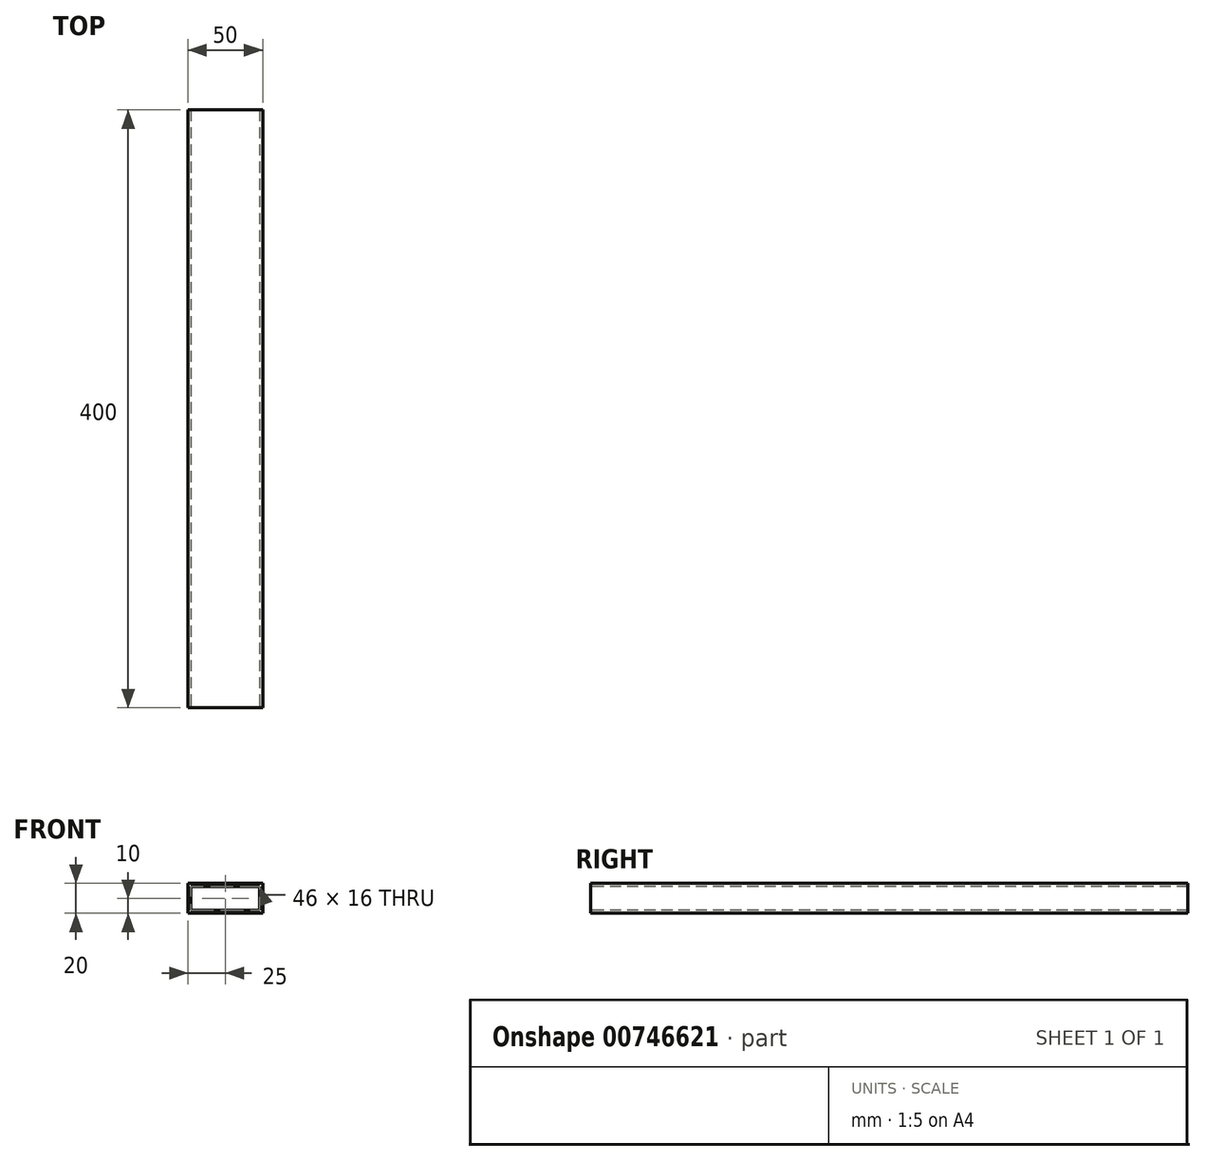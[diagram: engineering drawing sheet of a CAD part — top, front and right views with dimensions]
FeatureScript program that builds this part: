
annotation { "Feature Type Name" : "Feature", "Feature Type Description" : "" }
export const myFeature = defineFeature(function(context is Context, id is Id, definition is map)
    precondition{}
    {
        {
            var Q0;
            Q0=qCreatedBy(makeId("Front.planeOp"),FACE);
            var sketch = newSketch(context, id + "F0", { "sketchPlane" : qUnion([Q0])});
            skLineSegment(sketch, "E0.bottom", {"start": v(25, -10) * mm, "end": v(-25, -10) * mm});
            skLineSegment(sketch, "E0.top", {"start": v(25, 10) * mm, "end": v(-25, 10) * mm});
            skLineSegment(sketch, "E0.left", {"start": v(25, -10) * mm, "end": v(25, 10) * mm});
            skLineSegment(sketch, "E0.right", {"start": v(-25, -10) * mm, "end": v(-25, 10) * mm});
            skPoint(sketch, "E0.middle", {"position": v(0, 0) * mm});
            skLineSegment(sketch, "E1.bottom", {"start": v(-23, -8) * mm, "end": v(23, -8) * mm});
            skLineSegment(sketch, "E1.top", {"start": v(-23, 8) * mm, "end": v(23, 8) * mm});
            skLineSegment(sketch, "E1.left", {"start": v(-23, -8) * mm, "end": v(-23, 8) * mm});
            skLineSegment(sketch, "E1.right", {"start": v(23, -8) * mm, "end": v(23, 8) * mm});
            skSolve(sketch);
        }
        {
            var Q0;
            Q0=makeQuery(id+"F0.imprint","IMPRINT",FACE,{"disambiguationData":[TD([[makeQuery(id+"F0.imprint","IMPRINT",EDGE,{"derivedFrom":sQuery(id+"F0.wireOp",EDGE,"E0.bottom")}),-1.0]])]});
            extrude(context, id + "F1", {"entities" : qUnion([Q0]), "oppositeDirection" : true, "depth" : 400 * mm, "offsetDistance" : 25 * mm});
        }
    });
